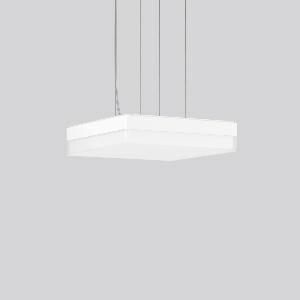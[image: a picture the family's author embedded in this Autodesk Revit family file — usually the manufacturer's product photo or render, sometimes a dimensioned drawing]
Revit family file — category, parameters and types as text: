
# Revit family: flat_slim_square_312541_002_bf27
name_source: partatom
category: Lighting Fixtures
units: mm (PartAtom-declared; Revit-internal decimal feet)

## family parameters
Cut with Voids When Loaded = No
Host = Face
Light Source = No
Part Type = Normal
Room Calculation Point = No
Round Connector Dimension = Use Diameter
Shared = No

## types (1)
- MultiLumen 2 840 (1 x LED Modul 840, 2300 lm, 4000)
    Apparent Load = 19 VA
    CIE Flux Codes = 43 74 93 92 100
    Color Rendering = 80
    Color Temperature = 4000
    Default Elevation = 1800 mm
    Height = 70 mm
    Lamp = 1 x LED Modul 840
    Lamp Light Flux = 2300 lm
    Lamp count = 1
    Length = 300 mm
    Lifetime = 50000 h
    Luminous efficacy = 121 lm/W
    Manufacturer = RZB
    ModVariant = No
    Model = 312541.002
    Mounting Place = Ceiling
    Mounting Type = Pendant
    Number of Poles = 1
    OnlyDefault = Yes
    Power Factor = 1
    Product Name = FLAT SLIM square
    Product group = Pendant luminaires
    ProductGroupID = 902
    Protection Class = Protection class I
    Protection Degree = IP 40
    RLX_Detail_Level = 1
    RLX_Emergency_Light_Flux = 0 lm
    RLX_Emergency_Type = 0
    RLX_Emergency_Type_DB = No
    RlxData = <blob elided: 14213 chars, md5=0b412819>
    Socket = socket
    Standby Power = 0 W
    System Light Flux = 2300 lm
    System Power = 19 W
    Type Comments = MultiLumen 2 840
    Type Image = 312541.002.jpg
    URL = http://relux.com
    VarID = multilumen_2_840
    Voltage = 230 V
    Voltage Range = 220-240 V
    Weight = 0.00 kg
    Width = 300 mm

## geometry (parser evidence)
native form markers: Sweep x13
no freeform markers — native parametric forms only
